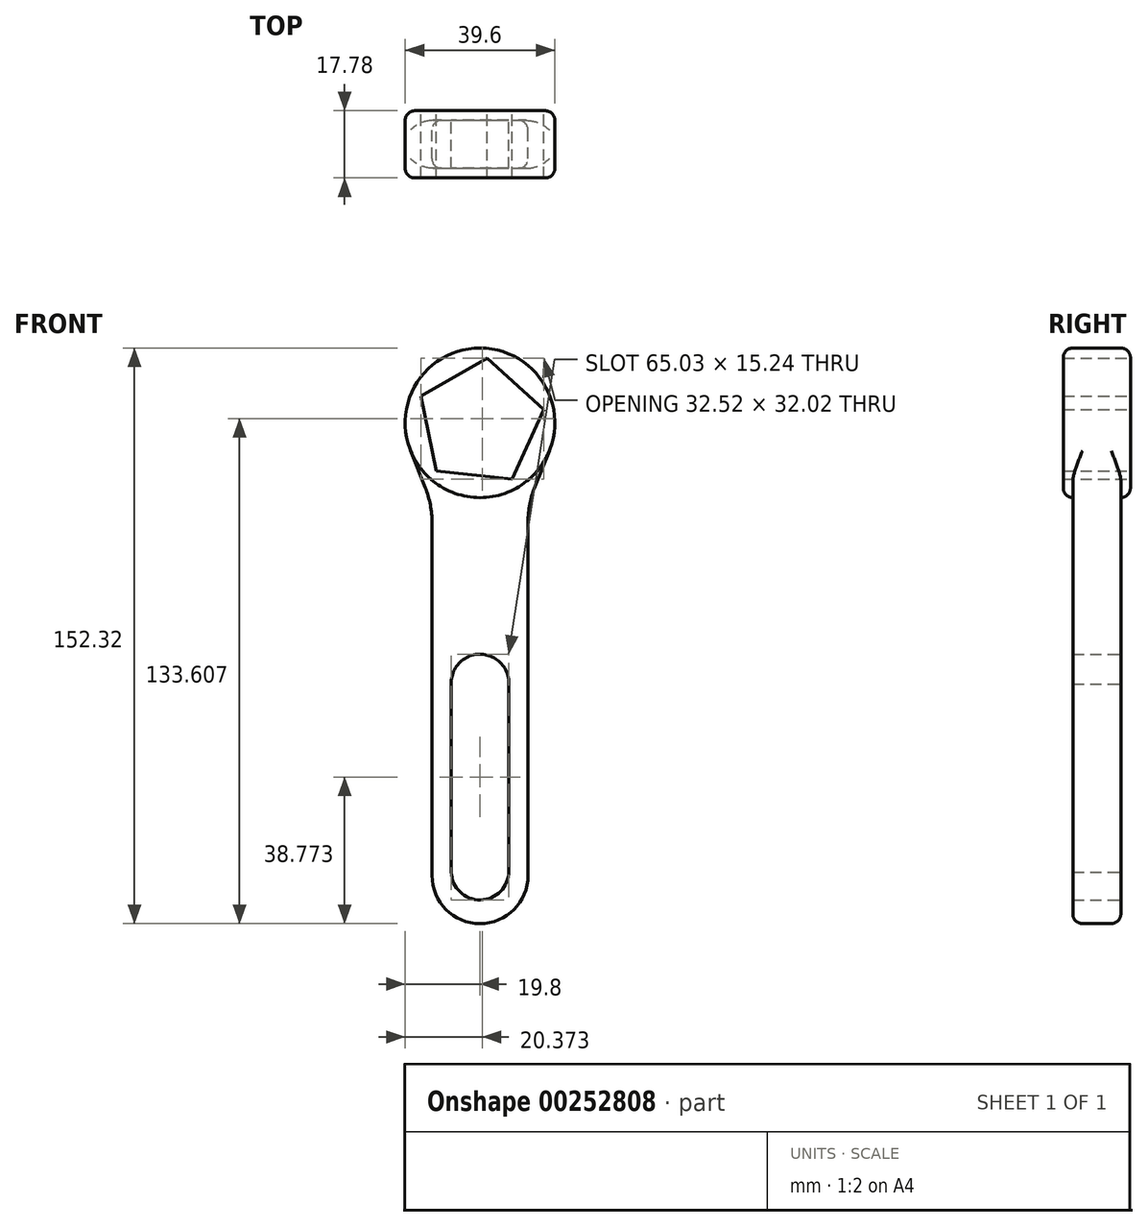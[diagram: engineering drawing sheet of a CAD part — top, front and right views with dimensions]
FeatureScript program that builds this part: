
annotation { "Feature Type Name" : "Feature", "Feature Type Description" : "" }
export const myFeature = defineFeature(function(context is Context, id is Id, definition is map)
    precondition{}
    {
        {
            var Q0;
            Q0=qCreatedBy(makeId("Front.planeOp"),FACE);
            var sketch = newSketch(context, id + "F0", { "sketchPlane" : qUnion([Q0])});
            skLineSegment(sketch, "E0", {"start": v(-12.7, 31.42) * mm, "end": v(-12.7, -61.89) * mm});
            skLineSegment(sketch, "E1", {"start": v(12.7, 31.58) * mm, "end": v(12.7, -61.89) * mm});
            skLineSegment(sketch, "E2", {"start": v(-0.2, -74.59) * mm, "end": v(-0.2, -74.59) * mm});
            skPoint(sketch, "E3.visualSharp", {"position": v(-12.7, -74.39) * mm});
            skArc(sketch, "E3.filletArc", {"start": v(-12.7, -61.89) * mm, "mid": v(-9.05, -70.8) * mm, "end": v(-0.2, -74.59) * mm});
            skPoint(sketch, "E4.visualSharp", {"position": v(12.7, -74.8) * mm});
            skArc(sketch, "E4.filletArc", {"start": v(-0.2, -74.59) * mm, "mid": v(8.9, -70.94) * mm, "end": v(12.7, -61.89) * mm});
            skCircle(sketch, "E5", {"center": v(0, 57.93) * mm, "radius": 19.8 * mm});
            skLineSegment(sketch, "E6", {"start": v(-14.5, 40.8) * mm, "end": v(-18.4, 50.62) * mm});
            skLineSegment(sketch, "E7", {"start": v(14.55, 41.1) * mm, "end": v(18.35, 50.51) * mm});
            skPoint(sketch, "E8.visualSharp", {"position": v(-12.7, 36.28) * mm});
            skArc(sketch, "E8.filletArc", {"start": v(-12.7, 31.42) * mm, "mid": v(-13.15, 36.2) * mm, "end": v(-14.5, 40.8) * mm});
            skPoint(sketch, "E9.visualSharp", {"position": v(12.7, 36.52) * mm});
            skArc(sketch, "E9.filletArc", {"start": v(14.55, 41.1) * mm, "mid": v(13.17, 36.43) * mm, "end": v(12.7, 31.58) * mm});
            skCircle(sketch, "E10.cCircle", {"center": v(0, 57.93) * mm, "radius": 13.91 * mm, "construction": true});
            skLineSegment(sketch, "E10.0", {"start": v(-15.69, 64.97) * mm, "end": v(1.85, 75.02) * mm});
            skLineSegment(sketch, "E10.1", {"start": v(1.85, 75.02) * mm, "end": v(16.83, 61.45) * mm});
            skLineSegment(sketch, "E10.2", {"start": v(16.83, 61.45) * mm, "end": v(8.55, 43) * mm});
            skLineSegment(sketch, "E10.3", {"start": v(8.55, 43) * mm, "end": v(-11.55, 45.19) * mm});
            skLineSegment(sketch, "E10.4", {"start": v(-11.55, 45.19) * mm, "end": v(-15.69, 64.97) * mm});
            skPoint(sketch, "E10.0.midPoint", {"position": v(-6.92, 70) * mm});
            skPoint(sketch, "E11.center.orphan", {"position": v(0, -11.07) * mm});
            skPoint(sketch, "E12.center.orphan", {"position": v(0, -62.88) * mm});
            skLineSegment(sketch, "E13", {"start": v(7.62, -10.92) * mm, "end": v(7.62, -60.71) * mm});
            skLineSegment(sketch, "E14", {"start": v(-7.62, -11.24) * mm, "end": v(-7.62, -60.92) * mm});
            skPoint(sketch, "E15.center.orphan", {"position": v(0, -65.81) * mm});
            skArc(sketch, "E16", {"start": v(7.62, -60.71) * mm, "mid": v(0.1, -68.33) * mm, "end": v(-7.62, -60.92) * mm});
            skArc(sketch, "E17", {"start": v(7.62, -10.92) * mm, "mid": v(-0.16, -3.3) * mm, "end": v(-7.62, -11.24) * mm});
            skSolve(sketch);
        }
        {
            var Q0;
            Q0=makeQuery(id+"F0.imprint","IMPRINT",FACE,{"disambiguationData":[TD([[makeQuery(id+"F0.imprint","IMPRINT",EDGE,{"derivedFrom":sQuery(id+"F0.wireOp",EDGE,"E0")}),1.0]])]});
            extrude(context, id + "F1", {"entities" : qUnion([Q0]), "endBound" : BoundingType.SYMMETRIC, "depth" : 12.7 * mm});
        }
        {
            var Q0;
            Q0=makeQuery(id+"F0.imprint","IMPRINT",FACE,{"disambiguationData":[TD([[makeQuery(id+"F0.imprint","IMPRINT",EDGE,{"derivedFrom":sQuery(id+"F0.wireOp",EDGE,"E10.0")}),1.0]])]});
            extrude(context, id + "F2", {"entities" : qUnion([Q0]), "operationType" : NewBodyOperationType.ADD, "endBound" : BoundingType.SYMMETRIC, "depth" : 17.78 * mm});
        }
        {
            var Q0;
            Q0=makeQuery(id+"F1.opExtrude","CAP_EDGE",EDGE,{"disambiguationData":[OSD([sQuery(id+"F0.wireOp",EDGE,"E0")])],"isStart":false});
            var Q1;
            Q1=makeQuery(id+"F1.opExtrude","CAP_EDGE",EDGE,{"disambiguationData":[OSD([sQuery(id+"F0.wireOp",EDGE,"E0")])],"isStart":true});
            var Q2;
            Q2=makeQuery(id+"F2.opExtrude","CAP_EDGE",EDGE,{"disambiguationData":[OSD([sQuery(id+"F0.wireOp",EDGE,"E5")])],"isStart":true});
            var Q3;
            Q3=makeQuery(id+"F2.opExtrude","CAP_EDGE",EDGE,{"disambiguationData":[OSD([sQuery(id+"F0.wireOp",EDGE,"E5")])],"isStart":false});
            fillet(context, id + "F3", {"entities" : qUnion([Q0, Q1, Q2, Q3]), "radius" : 2.54 * mm, "tangentPropagation" : true, "allowEdgeOverflow" : false});
        }
    });
